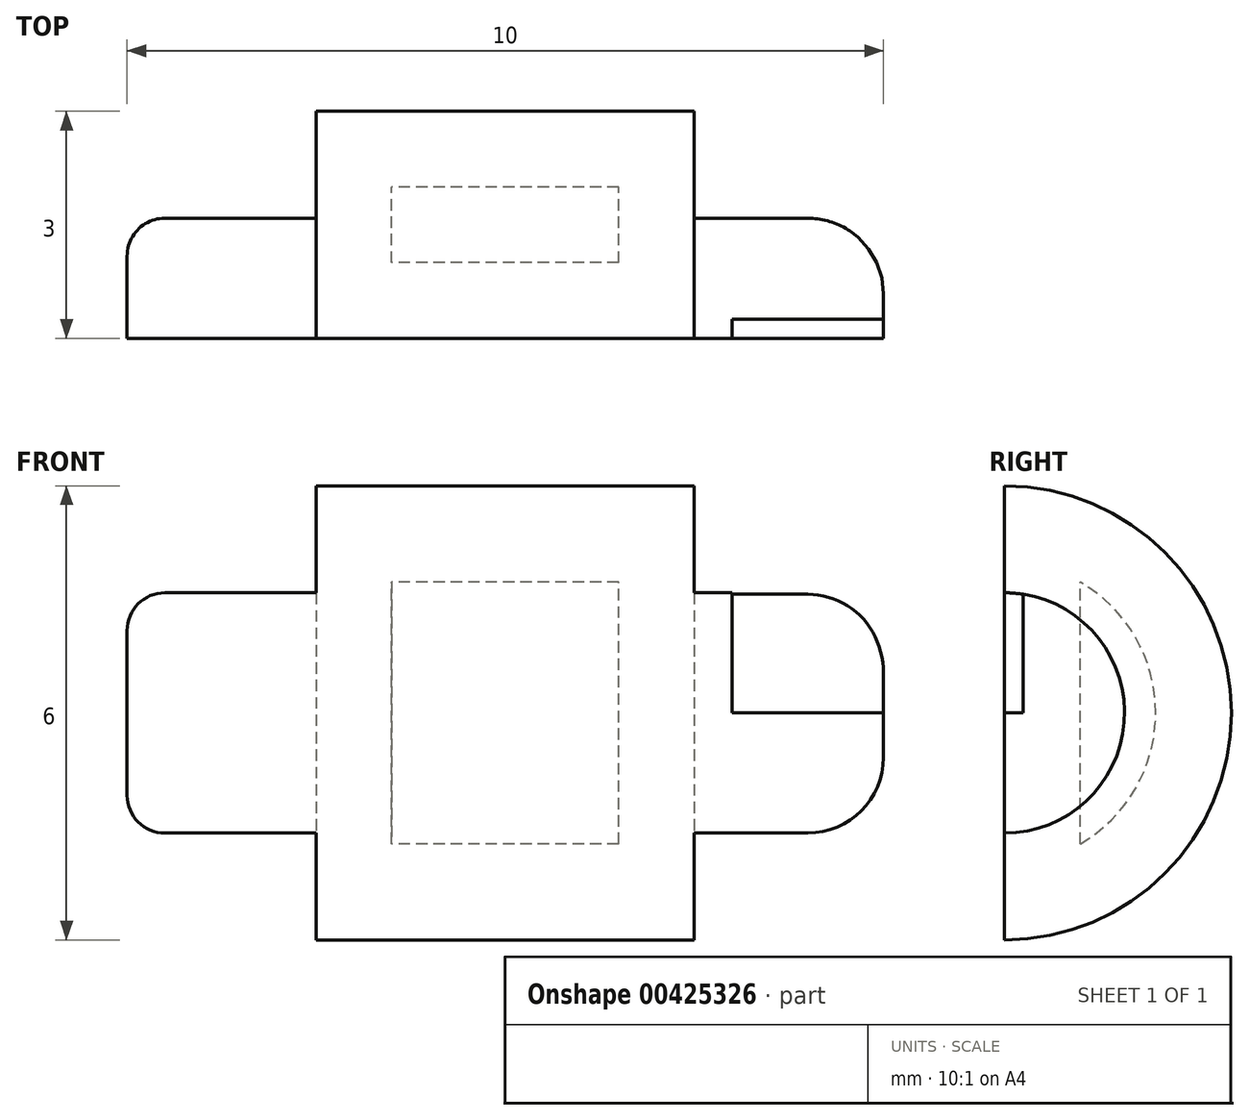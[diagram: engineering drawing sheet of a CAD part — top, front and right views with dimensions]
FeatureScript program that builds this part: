
annotation { "Feature Type Name" : "Feature", "Feature Type Description" : "" }
export const myFeature = defineFeature(function(context is Context, id is Id, definition is map)
    precondition{}
    {
        {
            var Q0;
            Q0=qCreatedBy(makeId("Top.planeOp"),FACE);
            var sketch = newSketch(context, id + "F0", { "sketchPlane" : qUnion([Q0])});
            skLineSegment(sketch, "E0", {"start": v(-3.83, 0) * mm, "end": v(4.32, 0) * mm, "construction": true});
            skLineSegment(sketch, "E1", {"start": v(-5, 1.59) * mm, "end": v(-2.5, 1.59) * mm});
            skLineSegment(sketch, "E2", {"start": v(-2.5, 1.59) * mm, "end": v(-2.5, 3) * mm});
            skLineSegment(sketch, "E3", {"start": v(-2.5, 3) * mm, "end": v(2.5, 3) * mm});
            skLineSegment(sketch, "E4", {"start": v(2.5, 3) * mm, "end": v(2.5, 1.59) * mm});
            skLineSegment(sketch, "E5", {"start": v(2.5, 1.59) * mm, "end": v(5, 1.59) * mm});
            skLineSegment(sketch, "E6", {"start": v(0, 0) * mm, "end": v(0, 5) * mm, "construction": true});
            skLineSegment(sketch, "E7", {"start": v(-5, 1.59) * mm, "end": v(-5, 0) * mm});
            skLineSegment(sketch, "E8", {"start": v(-5, 0) * mm, "end": v(5, 0) * mm});
            skLineSegment(sketch, "E9", {"start": v(5, 1.59) * mm, "end": v(5, 0) * mm});
            skSolve(sketch);
        }
        {
            var Q0;
            Q0 = qSketchRegion(id + "F0", true);
            var Q1;
            Q1=sQuery(id+"F0.wireOp",EDGE,"E0");
            revolve(context, id + "F1", {"entities" : qUnion([Q0]), "axis" : qUnion([Q1]), "revolveType" : RevolveType.SYMMETRIC, "angle" : 180 * degree});
        }
        {
            var Q0;
            Q0=makeQuery(id+"F1.opRevolve","SWEPT_FACE",FACE,{"disambiguationData":[OSD([sQuery(id+"F0.wireOp",EDGE,"E9")])]});
            var Q1;
            Q1=makeQuery(id+"F1.opRevolve","SWEPT_FACE",FACE,{"disambiguationData":[OSD([sQuery(id+"F0.wireOp",EDGE,"E7")])]});
            shell(context, id + "F2", {"entities" : qUnion([Q0, Q1]), "thickness" : 1 * mm});
        }
        {
            var Q0;
            Q0=makeQuery(id+"F1.opRevolve","SWEPT_EDGE",EDGE,{"disambiguationData":[OSD([sQuery(id+"F0.wireOp",EDGE,"E5"),sQuery(id+"F0.wireOp",EDGE,"E9")])]});
            fillet(context, id + "F3", {"entities" : qUnion([Q0]), "radius" : 1 * mm, "tangentPropagation" : true, "allowEdgeOverflow" : false});
        }
        {
            var Q0;
            Q0=makeQuery(id+"F1.opRevolve","SWEPT_EDGE",EDGE,{"disambiguationData":[OSD([sQuery(id+"F0.wireOp",EDGE,"E1"),sQuery(id+"F0.wireOp",EDGE,"E7")])]});
            fillet(context, id + "F4", {"entities" : qUnion([Q0]), "radius" : 0.5 * mm, "tangentPropagation" : true, "allowEdgeOverflow" : false});
        }
        {
            var Q0;
            Q0=qCreatedBy(makeId("Top.planeOp"),FACE);
            var sketch = newSketch(context, id + "F5", { "sketchPlane" : qUnion([Q0])});
            skLineSegment(sketch, "E10", {"start": v(0, 0) * mm, "end": v(6.31, 0) * mm, "construction": true});
            skLineSegment(sketch, "E11.bottom", {"start": v(3, -0.25) * mm, "end": v(7, -0.25) * mm});
            skLineSegment(sketch, "E11.top", {"start": v(3, 0.25) * mm, "end": v(7, 0.25) * mm});
            skLineSegment(sketch, "E11.left", {"start": v(3, -0.25) * mm, "end": v(3, 0.25) * mm});
            skLineSegment(sketch, "E11.right", {"start": v(7, -0.25) * mm, "end": v(7, 0.25) * mm});
            skPoint(sketch, "E11.middle", {"position": v(5, 0) * mm});
            skSolve(sketch);
        }
        {
            var Q0;
            Q0 = qSketchRegion(id + "F5", true);
            extrude(context, id + "F6", {"entities" : qUnion([Q0]), "operationType" : NewBodyOperationType.REMOVE, "depth" : 25 * mm, "offsetDistance" : 25 * mm});
        }
    });
